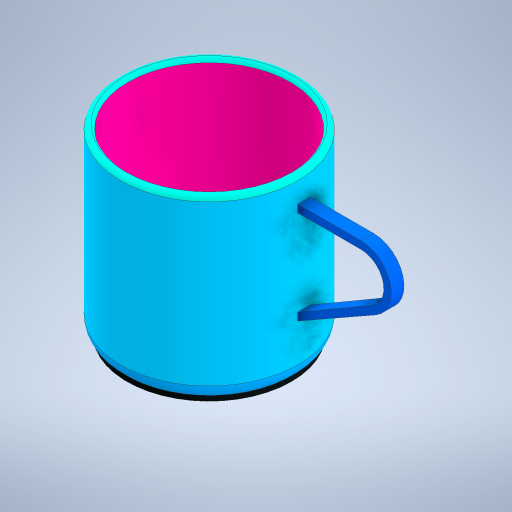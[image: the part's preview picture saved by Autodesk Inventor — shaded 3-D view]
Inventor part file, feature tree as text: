
AUTODESK INVENTOR PART (.ipt)
format: ipt  version: 2024 (Build 280153000, 153)  size: 327,680 bytes
history: native  units: mm
features: sketch x5, extrude x3, other x2, plane x2, revolve x1, shell x1, fillet x1
ambient origin geometry x8: Origin, YZ Plane, XZ Plane, XY Plane, X Axis, Y Axis, Z Axis, Center Point
bodies: Body1 (feature_tree)
feature tree (15):
  other  "Sección transversal1"
  other  "Sólido1"
  revolve  "Revolución1"  [1 undecoded]
  shell  "Vaciado2"  Thickness=10.0mm
  sketch  "Boceto2"  dims[d7=0.5mm d8=2.0mm d9=0.0mm d10=20.0mm d11=10.0mm]
  plane  "Plano de trabajo7"
  plane  "Plano de trabajo8"
  extrude  "Extrusión1"  Depth=15.0mm
  sketch  "Boceto5"  dims[d12=25.0mm d13=15.0mm]
  extrude  "Extrusión2"  Depth=5.0mm TaperAngle=0.0deg
  fillet  "Empalme1"  Radius=3.0mm
  extrude  "Extrusión3"  Depth=3.0mm
  sketch  "Boceto1"  dims[d4=360.0deg d6=3.0mm]
  sketch  "Boceto6"  dims[d20=12.0mm d21=5.0mm d22=0.0mm d23=3.0mm]
  sketch  "Boceto7"  dims[d24=3.0mm d26=3.0mm d27=3.0mm d28=3.0mm d29=25.0mm d30=9.0mm d31=5.0mm d32=0.0mm d33=2.0mm d34=65.0mm d35=62.0mm d36=2.0mm d37=0.0mm]
note: 1 required parameter value undecoded (feature->parameter linkage not recoverable at this tier; creation-order binding heuristic only, values carry confidence <= 0.55)
